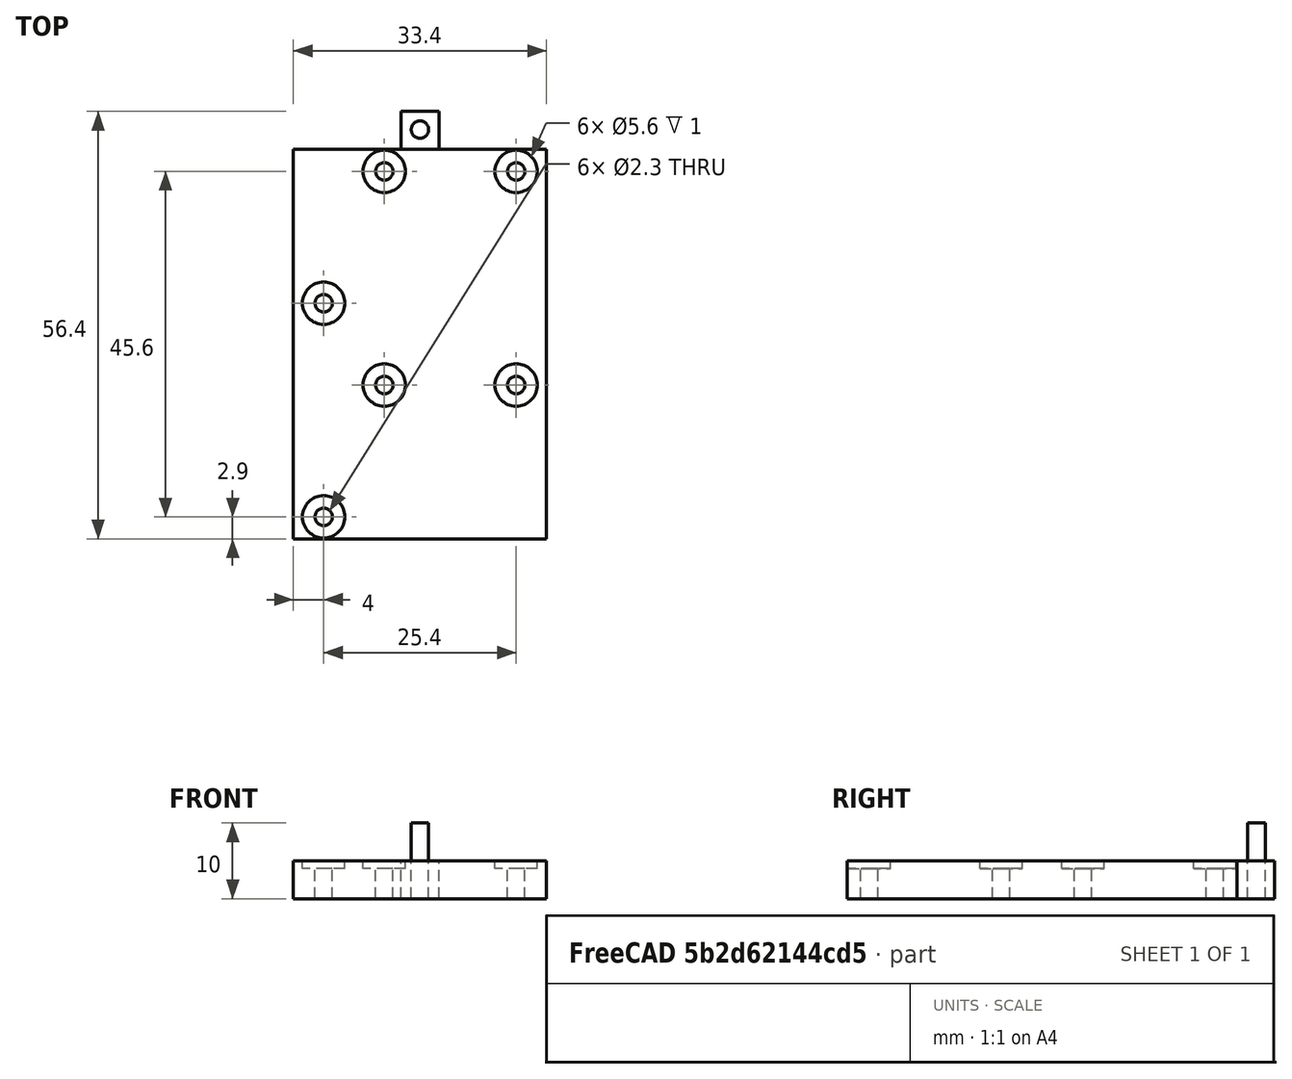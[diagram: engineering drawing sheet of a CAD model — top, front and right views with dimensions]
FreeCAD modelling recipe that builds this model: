
FCSTD DOCUMENT
Label: servoPusherHolderSlide
objects: Part::Cylinder×13, Part::Cut×12, Part::Box×2
note: 27 computed .brp shape members not serialized (recipe doc carries the construction recipe); baked Part::Feature solids carry a one-line shape summary decoded from their .brp

FEATURE [Part::Box] Box
  Height = 5
  Length = 33.4
  Width = 51.4
FEATURE [Part::Cylinder] Cylinder
  Angle = 360
  Height = 1
  Placement = pos=(4,2.9,4) rot=(0,0,1;0rad)
  Radius = 2.8
FEATURE [Part::Cylinder] Cylinder001
  Angle = 360
  Height = 10
  Placement = pos=(4,2.9,0) rot=(0,0,1;0rad)
  Radius = 1.15
FEATURE [Part::Cylinder] Cylinder002
  Angle = 360
  Height = 1
  Placement = pos=(4,31.1,4) rot=(0,0,1;0rad)
  Radius = 2.8
FEATURE [Part::Cylinder] Cylinder001001
  Angle = 360
  Height = 10
  Placement = pos=(4,31.1,0) rot=(0,0,1;0rad)
  Radius = 1.15
FEATURE [Part::Cylinder] Cylinder002001
  Angle = 360
  Height = 1
  Placement = pos=(12,20.3,4) rot=(0,0,1;0rad)
  Radius = 2.8
FEATURE [Part::Cylinder] Cylinder001001001
  Angle = 360
  Height = 10
  Placement = pos=(12,20.3,0) rot=(0,0,1;0rad)
  Radius = 1.15
FEATURE [Part::Cylinder] Cylinder002001001
  Angle = 360
  Height = 1
  Placement = pos=(12,48.5,4) rot=(0,0,1;0rad)
  Radius = 2.8
FEATURE [Part::Cylinder] Cylinder001001001001
  Angle = 360
  Height = 10
  Placement = pos=(12,48.5,0) rot=(0,0,1;0rad)
  Radius = 1.15
FEATURE [Part::Cylinder] Cylinder002001001001
  Angle = 360
  Height = 1
  Placement = pos=(29.4,48.5,4) rot=(0,0,1;0rad)
  Radius = 2.8
FEATURE [Part::Cylinder] Cylinder001001001001001
  Angle = 360
  Height = 10
  Placement = pos=(29.4,48.5,0) rot=(0,0,1;0rad)
  Radius = 1.15
FEATURE [Part::Cylinder] Cylinder002001001002
  Angle = 360
  Height = 1
  Placement = pos=(29.4,20.3,4) rot=(0,0,1;0rad)
  Radius = 2.8
FEATURE [Part::Cylinder] Cylinder001001001001002
  Angle = 360
  Height = 10
  Placement = pos=(29.4,20.3,0) rot=(0,0,1;0rad)
  Radius = 1.15
FEATURE [Part::Cut] Cut
  Base = -> Box
  Tool = -> Cylinder
FEATURE [Part::Cut] Cut001
  Base = -> Cut
  Tool = -> Cylinder001001001001002
FEATURE [Part::Cut] Cut002
  Base = -> Cut001
  Tool = -> Cylinder002001001002
FEATURE [Part::Cut] Cut003
  Base = -> Cut002
  Tool = -> Cylinder001001001001001
FEATURE [Part::Cut] Cut004
  Base = -> Cut003
  Tool = -> Cylinder002001001001
FEATURE [Part::Cut] Cut005
  Base = -> Cut004
  Tool = -> Cylinder001001001001
FEATURE [Part::Cut] Cut006
  Base = -> Cut005
  Tool = -> Cylinder002001001
FEATURE [Part::Cut] Cut007
  Base = -> Cut006
  Tool = -> Cylinder001001001
FEATURE [Part::Cut] Cut008
  Base = -> Cut007
  Tool = -> Cylinder002001
FEATURE [Part::Cut] Cut009
  Base = -> Cut008
  Tool = -> Cylinder001001
FEATURE [Part::Cut] Cut010
  Base = -> Cut009
  Tool = -> Cylinder002
FEATURE [Part::Cut] Cut011
  Base = -> Cut010
  Tool = -> Cylinder001
FEATURE [Part::Box] Box001
  Height = 5
  Length = 5
  Placement = pos=(14.2,51.4,0) rot=(0,0,1;0rad)
  Width = 5
FEATURE [Part::Cylinder] Cylinder001001001001003
  Angle = 360
  Height = 10
  Placement = pos=(16.7,54,0) rot=(0,0,1;0rad)
  Radius = 1.15
